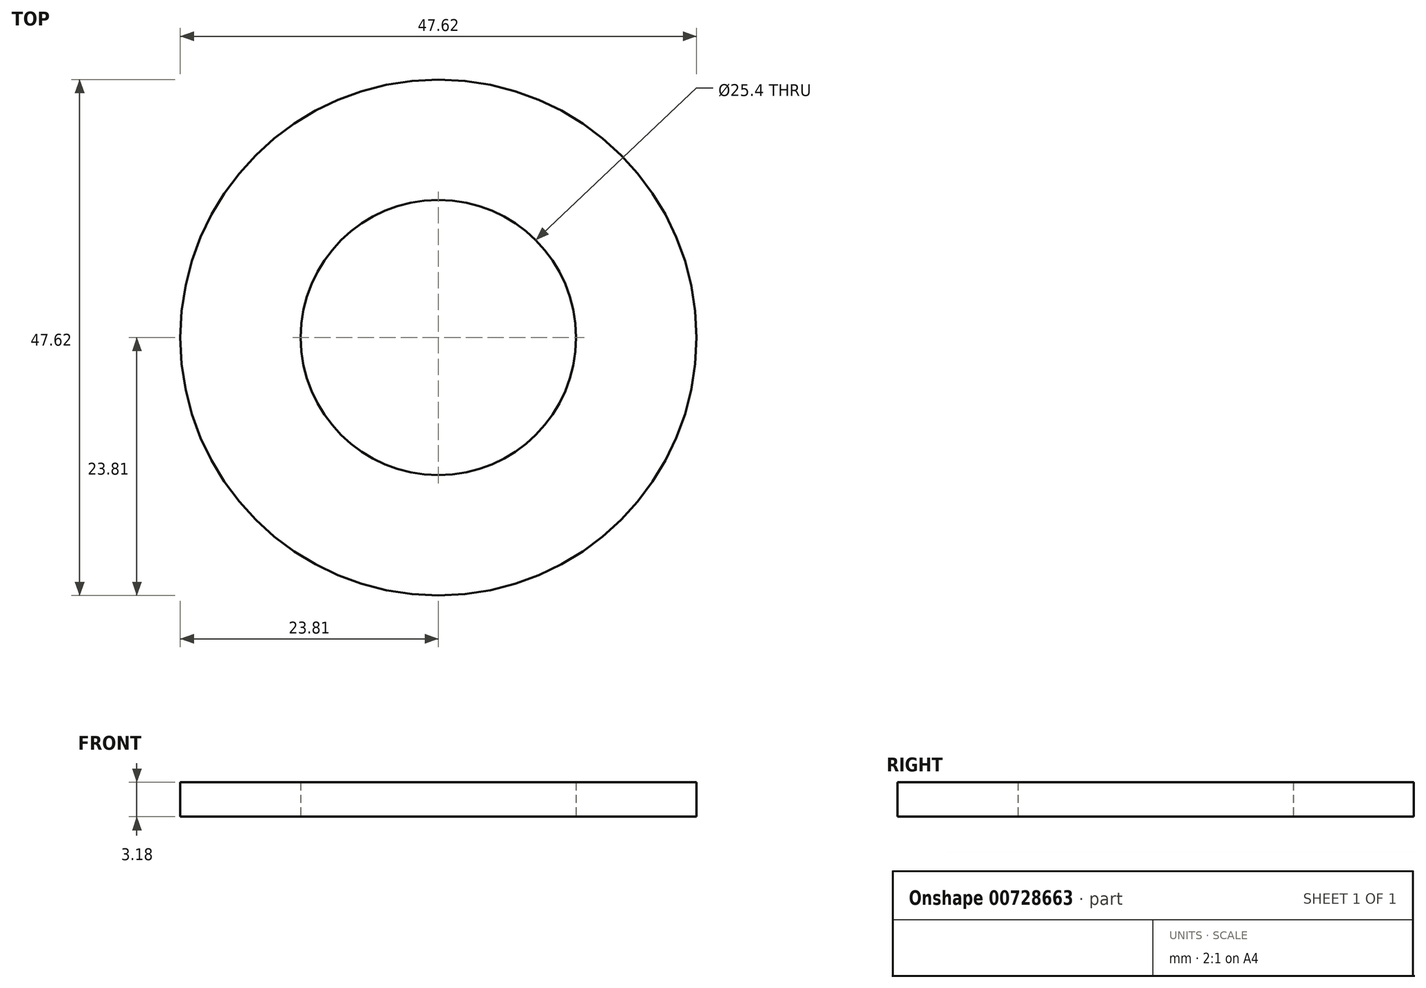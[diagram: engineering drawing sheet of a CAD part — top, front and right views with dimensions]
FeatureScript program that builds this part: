
annotation { "Feature Type Name" : "Feature", "Feature Type Description" : "" }
export const myFeature = defineFeature(function(context is Context, id is Id, definition is map)
    precondition{}
    {
        {
            var Q0;
            Q0=qCreatedBy(makeId("Top.planeOp"),FACE);
            var sketch = newSketch(context, id + "F0", { "sketchPlane" : qUnion([Q0])});
            skCircle(sketch, "E0", {"center": v(0, 0) * mm, "radius": 23.81 * mm});
            skCircle(sketch, "E1", {"center": v(0, 0) * mm, "radius": 12.7 * mm});
            skSolve(sketch);
        }
        {
            var Q0;
            Q0=makeQuery(id+"F0.imprint","IMPRINT",FACE,{"disambiguationData":[TD([[makeQuery(id+"F0.imprint","IMPRINT",EDGE,{"derivedFrom":sQuery(id+"F0.wireOp",EDGE,"E0")}),1.0]])]});
            extrude(context, id + "F1", {"entities" : qUnion([Q0]), "depth" : 3.17 * mm, "offsetDistance" : 25.4 * mm});
        }
    });
